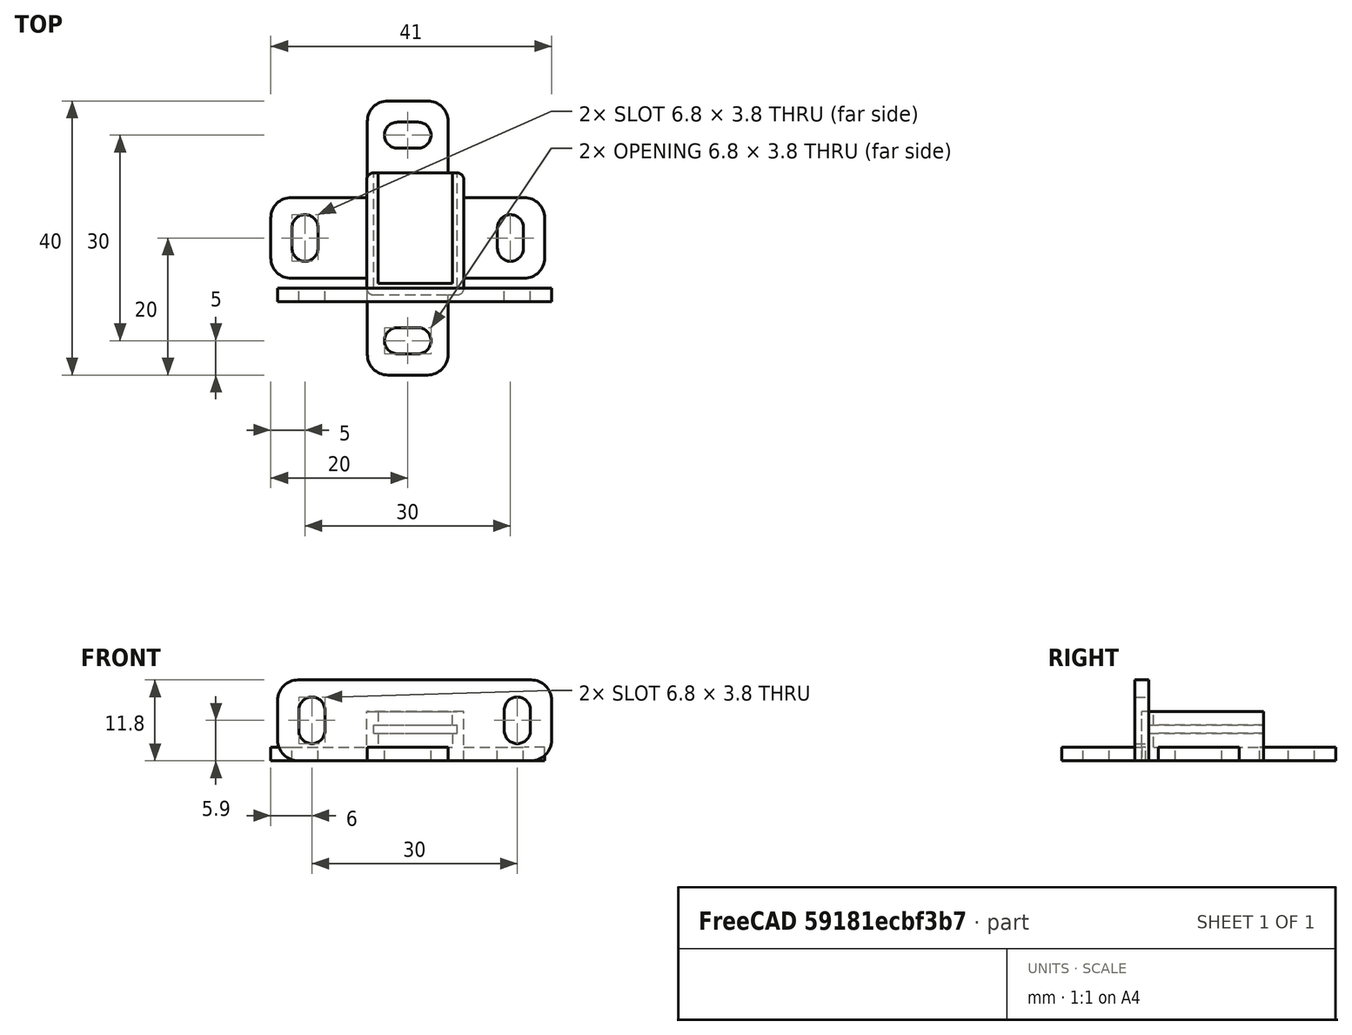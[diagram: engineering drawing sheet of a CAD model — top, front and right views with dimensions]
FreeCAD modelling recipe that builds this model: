
FCSTD DOCUMENT  (FreeCAD 0.19R23578 (Git))
Label: kxd10036
License: FreeArt
LicenseURL: http://artlibre.org/licence/lal
objects: Part::Box×9, Part::MultiFuse×6, Part::Fillet×3, Part::Feature×3, Part::Cut×3, App::Part×3, Spreadsheet::Sheet×1
note: 24 computed .brp shape members not serialized (recipe doc carries the construction recipe); baked Part::Feature solids carry a one-line shape summary decoded from their .brp

FEATURE [Spreadsheet::Sheet] Spreadsheet  label="p"
  cells = A1=pcb_x; B1(pcb_x)=12.2; A2=pcb_y; B2(pcb_y)=16.8; A3=pcb_z; B3(pcb_z)=1.2; A4=pcb_under; B4(pcb_under)=2; A5=side_wall; B5(side_wall)=1; A6=pcb_side_lane; B6(pcb_side_lane)=0.7; A7=bottom_wall; B7(bottom_wall)=2; A8=pcb_above; B8(pcb_above)=2; A9=box_x; B9(box_x)==pcb_x + 2 * side_wall; A10=box_y; B10(box_y)==pcb_y + side_wall; A11=box_z; B11(box_z)==bottom_wall + pcb_under + pcb_z + pcb_above
FEATURE [Part::Box] Box  label="external cube"
  AttacherType = Attacher::AttachEngine3D
  Height = 7.2
  Length = 14.2
  Width = 17.8
  expr: Length = <<p>>.box_x
  expr: Width = <<p>>.box_y
  expr: Height = <<p>>.box_z
FEATURE [Part::Box] Box006  label="internal cube"
  AttacherType = Attacher::AttachEngine3D
  Height = 5.2
  Length = 10.8
  Placement = pos=(1.7,1.7,2) rot=(0,0,1;0rad)
  Width = 16.4
  expr: Length = <<p>>.pcb_x - 2 * <<p>>.pcb_side_lane
  expr: Width = <<p>>.pcb_y - 2 * <<p>>.pcb_side_lane + <<p>>.side_wall
  expr: Height = <<p>>.pcb_under + <<p>>.pcb_z + <<p>>.pcb_above
  expr: .Placement.Base.z = <<p>>.bottom_wall
  expr: .Placement.Base.x = <<p>>.side_wall + <<p>>.pcb_side_lane
  expr: .Placement.Base.y = <<p>>.side_wall + <<p>>.pcb_side_lane
FEATURE [Part::Box] Box007  label="pcb extract cube"
  AttacherType = Attacher::AttachEngine3D
  Height = 1.2
  Length = 12.2
  Placement = pos=(1,1,4) rot=(0,0,1;0rad)
  Width = 16.8
  expr: Height = <<p>>.pcb_z
  expr: .Placement.Base.z = <<p>>.bottom_wall + <<p>>.pcb_under
  expr: Width = <<p>>.pcb_y
  expr: Length = <<p>>.pcb_x
  expr: .Placement.Base.x = <<p>>.side_wall
  expr: .Placement.Base.y = <<p>>.side_wall
FEATURE [Part::MultiFuse] Fusion  label="extract fusion"
  Shapes = -> [Box006,Box007]
FEATURE [Part::Fillet] Fillet  label="external fillet"
  Base = -> Box
  Edges = 4 edges r=1: [Edge1,Edge3,Edge5,Edge7]
FEATURE [Part::Box] Box008  label="external cube001"
  AttacherType = Attacher::AttachEngine3D
  Height = 7.2
  Length = 14.2
  Width = 17.8
  expr: Length = <<p>>.box_x
  expr: Width = <<p>>.box_y
  expr: Height = <<p>>.box_z
FEATURE [Part::Fillet] Fillet001  label="external fillet001"
  Base = -> Box008
  Edges = 4 edges r=1: [Edge1,Edge3,Edge5,Edge7]
FEATURE [Part::Box] Box009  label="internal cube001"
  AttacherType = Attacher::AttachEngine3D
  Height = 5.2
  Length = 10.8
  Placement = pos=(1.7,1.7,2) rot=(0,0,1;0rad)
  Width = 16.4
  expr: Length = <<p>>.pcb_x - 2 * <<p>>.pcb_side_lane
  expr: Width = <<p>>.pcb_y - 2 * <<p>>.pcb_side_lane + <<p>>.side_wall
  expr: Height = <<p>>.pcb_under + <<p>>.pcb_z + <<p>>.pcb_above
  expr: .Placement.Base.z = <<p>>.bottom_wall
  expr: .Placement.Base.x = <<p>>.side_wall + <<p>>.pcb_side_lane
  expr: .Placement.Base.y = <<p>>.side_wall + <<p>>.pcb_side_lane
FEATURE [Part::Box] Box010  label="pcb extract cube001"
  AttacherType = Attacher::AttachEngine3D
  Height = 1.2
  Length = 12.2
  Placement = pos=(1,1,4) rot=(0,0,1;0rad)
  Width = 16.8
  expr: Height = <<p>>.pcb_z
  expr: .Placement.Base.z = <<p>>.bottom_wall + <<p>>.pcb_under
  expr: Width = <<p>>.pcb_y
  expr: Length = <<p>>.pcb_x
  expr: .Placement.Base.x = <<p>>.side_wall
  expr: .Placement.Base.y = <<p>>.side_wall
FEATURE [Part::MultiFuse] Fusion003  label="extract fusion001"
  Shapes = -> [Box009,Box010]
FEATURE [Part::Box] Box011  label="external cube002"
  AttacherType = Attacher::AttachEngine3D
  Height = 7.2
  Length = 14.2
  Width = 17.8
  expr: Height = <<p>>.box_z
  expr: Width = <<p>>.box_y
  expr: Length = <<p>>.box_x
FEATURE [Part::Fillet] Fillet002  label="external fillet002"
  Base = -> Box011
  Edges = 4 edges r=1: [Edge1,Edge3,Edge5,Edge7]
FEATURE [Part::Box] Box012  label="internal cube002"
  AttacherType = Attacher::AttachEngine3D
  Height = 5.2
  Length = 10.8
  Placement = pos=(1.7,1.7,2) rot=(0,0,1;0rad)
  Width = 16.4
  expr: .Placement.Base.y = <<p>>.side_wall + <<p>>.pcb_side_lane
  expr: .Placement.Base.x = <<p>>.side_wall + <<p>>.pcb_side_lane
  expr: .Placement.Base.z = <<p>>.bottom_wall
  expr: Height = <<p>>.pcb_under + <<p>>.pcb_z + <<p>>.pcb_above
  expr: Width = <<p>>.pcb_y - 2 * <<p>>.pcb_side_lane + <<p>>.side_wall
  expr: Length = <<p>>.pcb_x - 2 * <<p>>.pcb_side_lane
FEATURE [Part::Box] Box013  label="pcb extract cube002"
  AttacherType = Attacher::AttachEngine3D
  Height = 1.2
  Length = 12.2
  Placement = pos=(1,1,4) rot=(0,0,1;0rad)
  Width = 16.8
  expr: .Placement.Base.y = <<p>>.side_wall
  expr: .Placement.Base.x = <<p>>.side_wall
  expr: Length = <<p>>.pcb_x
  expr: Width = <<p>>.pcb_y
  expr: .Placement.Base.z = <<p>>.bottom_wall + <<p>>.pcb_under
  expr: Height = <<p>>.pcb_z
FEATURE [Part::MultiFuse] Fusion005  label="extract fusion002"
  Shapes = -> [Box012,Box013]
FEATURE [Part::Feature] Cut002001  label="attach plane y dir002"
  Placement = pos=(0.1,-11.7,0) rot=(0,0,1;0rad)
  shape: bbox 11.8 x 40 x 2 mm, 20 faces (baked)
FEATURE [Part::MultiFuse] Fusion002  label="outer fusion001"
  Shapes = -> [Fillet001,Cut002001]
FEATURE [Part::Cut] Cut003003  label="body cut y"
  Base = -> Fusion002
  Tool = -> Fusion003
FEATURE [App::Part] Part001  label="kxd10036 pcb box y part"
  Group = -> [Fusion003,Box010,Fillet001,Box008,Fusion002,Box009,Cut003003]
  Origin = -> Origin001
FEATURE [Part::Feature] Cut003009  label="attach plane x dir002"
  Placement = pos=(-14,2.4,0) rot=(0,0,1;0rad)
  shape: bbox 40 x 11.8 x 2 mm, 18 faces (baked)
FEATURE [Part::MultiFuse] Fusion001  label="outer fusion"
  Shapes = -> [Fillet,Cut003009]
FEATURE [Part::Cut] Cut  label="body cut"
  Base = -> Fusion001
  Tool = -> Fusion
FEATURE [App::Part] Part  label="kxd10036 pcb box part"
  Group = -> [Box006,Box007,Fusion,Cut]
  Origin = -> Origin
FEATURE [Part::Feature] Cut003010  label="attach plane x dir003"
  Placement = pos=(-13,-1,11.8) rot=(-1,0,0;1.5708rad)
  shape: bbox 40 x 2 x 11.8 mm, 18 faces (baked)
FEATURE [Part::MultiFuse] Fusion004  label="outer fusion002"
  Shapes = -> [Fillet002,Cut003010]
FEATURE [Part::Cut] Cut003004  label="body cut z"
  Base = -> Fusion004
  Tool = -> Fusion005
FEATURE [App::Part] Part002  label="kxd10036 pcb box z part"
  Group = -> [Fusion005,Box013,Fillet002,Box011,Fusion004,Box012,Cut003004]
  Origin = -> Origin002
